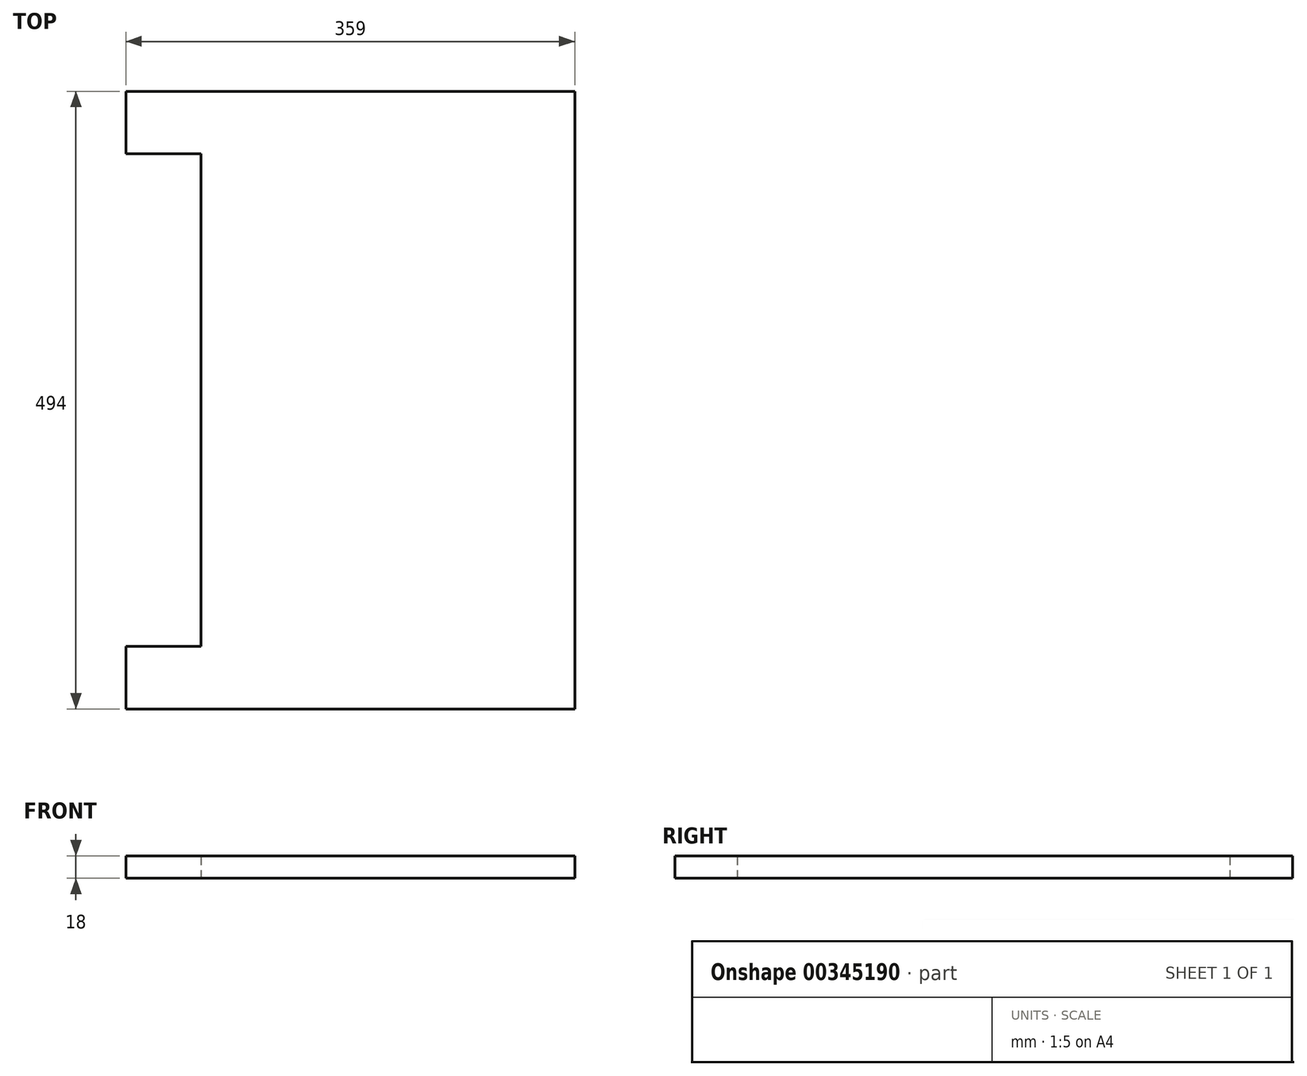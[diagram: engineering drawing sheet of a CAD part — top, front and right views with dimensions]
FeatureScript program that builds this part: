
annotation { "Feature Type Name" : "Feature", "Feature Type Description" : "" }
export const myFeature = defineFeature(function(context is Context, id is Id, definition is map)
    precondition{}
    {
        {
            var Q0;
            Q0=qCreatedBy(makeId("Top.planeOp"),FACE);
            var sketch = newSketch(context, id + "F0", { "sketchPlane" : qUnion([Q0])});
            skLineSegment(sketch, "E0", {"start": v(0, 0) * mm, "end": v(359, 0) * mm});
            skLineSegment(sketch, "E1", {"start": v(359, 0) * mm, "end": v(359, 494) * mm});
            skLineSegment(sketch, "E2", {"start": v(359, 494) * mm, "end": v(0, 494) * mm});
            skLineSegment(sketch, "E3", {"start": v(0, 494) * mm, "end": v(0, 444) * mm});
            skLineSegment(sketch, "E4", {"start": v(0, 444) * mm, "end": v(60, 444) * mm});
            skLineSegment(sketch, "E5", {"start": v(60, 444) * mm, "end": v(60, 50) * mm});
            skLineSegment(sketch, "E6", {"start": v(60, 50) * mm, "end": v(0, 50) * mm});
            skLineSegment(sketch, "E7", {"start": v(0, 50) * mm, "end": v(0, 0) * mm});
            skSolve(sketch);
        }
        {
            var Q0;
            Q0=makeQuery(id+"F0.imprint","IMPRINT",FACE,{"disambiguationData":[TD([[makeQuery(id+"F0.imprint","IMPRINT",EDGE,{"derivedFrom":sQuery(id+"F0.wireOp",EDGE,"E0")}),1.0]])]});
            extrude(context, id + "F1", {"entities" : qUnion([Q0]), "depth" : 18 * mm});
        }
    });
